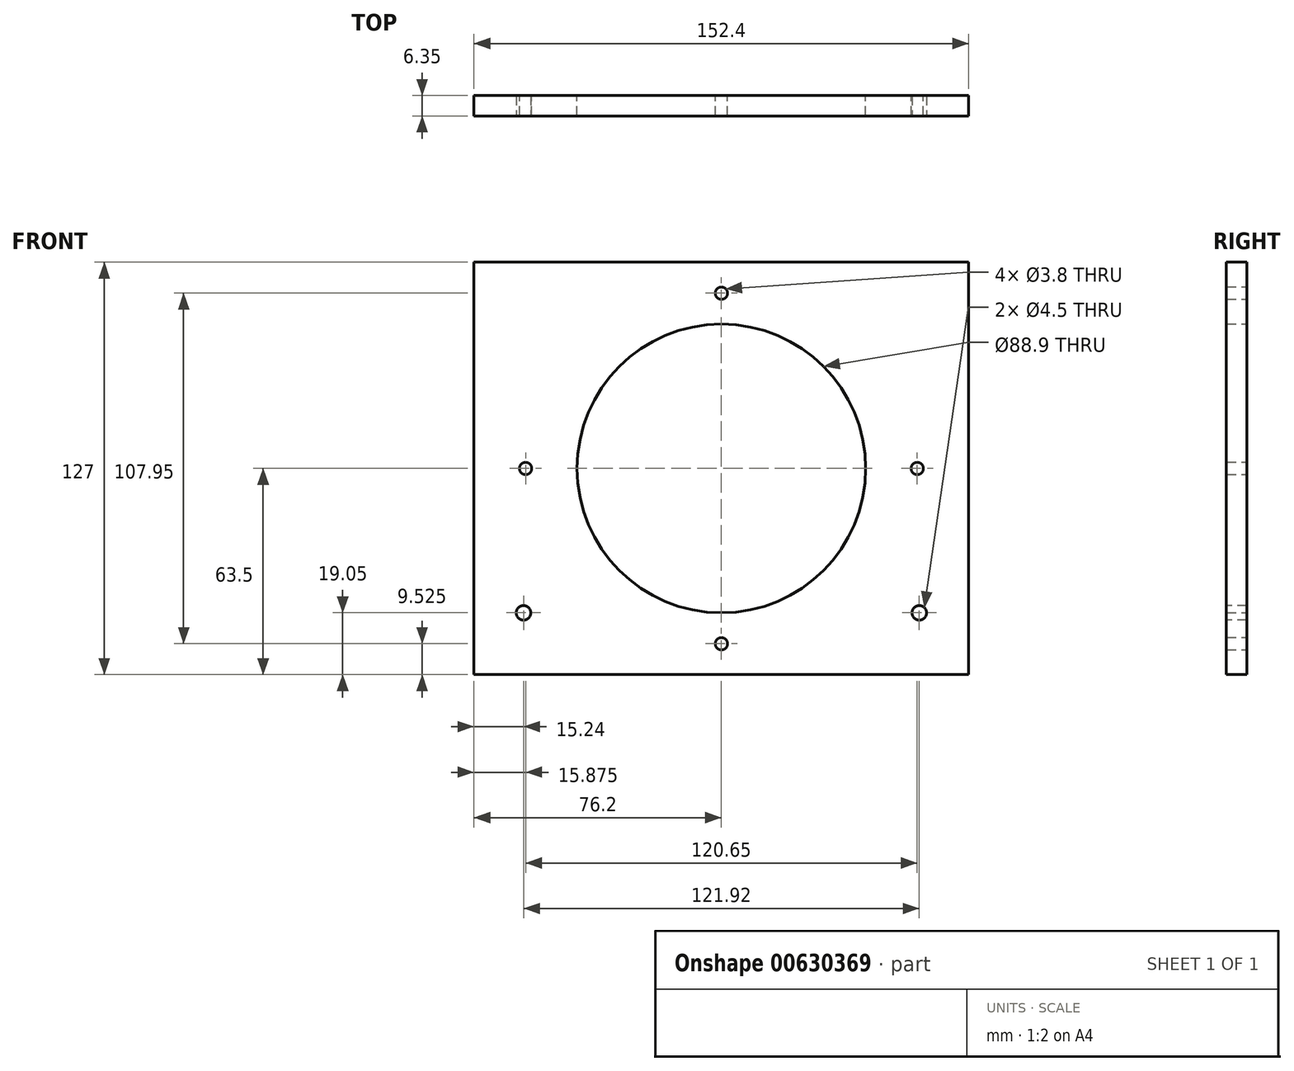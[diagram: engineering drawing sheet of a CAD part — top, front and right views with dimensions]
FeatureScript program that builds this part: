
annotation { "Feature Type Name" : "Feature", "Feature Type Description" : "" }
export const myFeature = defineFeature(function(context is Context, id is Id, definition is map)
    precondition{}
    {
        {
            var Q0;
            Q0=qCreatedBy(makeId("Front.planeOp"),FACE);
            var sketch = newSketch(context, id + "F0", { "sketchPlane" : qUnion([Q0])});
            skCircle(sketch, "E0", {"center": v(0, 0) * mm, "radius": 44.45 * mm});
            skLineSegment(sketch, "E1.bottom", {"start": v(-76.2, 63.5) * mm, "end": v(76.2, 63.5) * mm});
            skLineSegment(sketch, "E1.top", {"start": v(-76.2, -63.5) * mm, "end": v(76.2, -63.5) * mm});
            skLineSegment(sketch, "E1.left", {"start": v(-76.2, 63.5) * mm, "end": v(-76.2, -63.5) * mm});
            skLineSegment(sketch, "E1.right", {"start": v(76.2, 63.5) * mm, "end": v(76.2, -63.5) * mm});
            skSolve(sketch);
        }
        {
            var Q0;
            Q0 = qSketchRegion(id + "F0", true);
            extrude(context, id + "F1", {"entities" : qUnion([Q0]), "depth" : 6.35 * mm, "offsetDistance" : 25.4 * mm});
        }
        {
            var Q0;
            Q0=makeQuery(id+"F1.opExtrude","CAP_FACE",FACE,{"disambiguationData":[OSD([sQuery(id+"F0.wireOp",EDGE,"E0"),sQuery(id+"F0.wireOp",EDGE,"E1.bottom"),sQuery(id+"F0.wireOp",EDGE,"E1.top"),sQuery(id+"F0.wireOp",EDGE,"E1.left"),sQuery(id+"F0.wireOp",EDGE,"E1.right")])],"isStart":true});
            var sketch = newSketch(context, id + "F2", { "sketchPlane" : qUnion([Q0])});
            skSolve(sketch);
        }
        {
            var Q0;
            Q0=makeQuery(id+"F2.imprint","IMPRINT",FACE,{"disambiguationData":[TD([[makeQuery(id+"F2.imprint","IMPRINT",EDGE,{"derivedFrom":makeQuery(id+"F1.opExtrude","CAP_EDGE",EDGE,{"disambiguationData":[OSD([sQuery(id+"F0.wireOp",EDGE,"E0")])],"isStart":true})}),1.0]])]});
            var sketch = newSketch(context, id + "F3", { "sketchPlane" : qUnion([Q0])});
            skLineSegment(sketch, "E2", {"start": v(0, 63.5) * mm, "end": v(0, 44.45) * mm, "construction": true});
            skLineSegment(sketch, "E3", {"start": v(-76.2, 0) * mm, "end": v(-44.45, 0) * mm, "construction": true});
            skLineSegment(sketch, "E4", {"start": v(44.45, 0) * mm, "end": v(76.2, 0) * mm, "construction": true});
            skLineSegment(sketch, "E5", {"start": v(0, -63.5) * mm, "end": v(0, -44.45) * mm, "construction": true});
            skPoint(sketch, "E6", {"position": v(0, 53.98) * mm});
            skPoint(sketch, "E7", {"position": v(60.32, 0) * mm});
            skPoint(sketch, "E8", {"position": v(0, -53.98) * mm});
            skPoint(sketch, "E9", {"position": v(-60.32, 0) * mm});
            skSolve(sketch);
        }
        {
            var Q0;
            Q0=sQuery(id+"F3.wireOp",VERTEX,"E9");
            var Q1;
            Q1=sQuery(id+"F3.wireOp",VERTEX,"E6");
            var Q2;
            Q2=sQuery(id+"F3.wireOp",VERTEX,"E7");
            var Q3;
            Q3=sQuery(id+"F3.wireOp",VERTEX,"E8");
            var Q4;
            Q4=makeQuery(id+"F1.opExtrude","SWEPT_BODY",BODY,{"disambiguationData":[OSD([sQuery(id+"F0.wireOp",EDGE,"E0"),sQuery(id+"F0.wireOp",EDGE,"E1.bottom"),sQuery(id+"F0.wireOp",EDGE,"E1.top"),sQuery(id+"F0.wireOp",EDGE,"E1.left"),sQuery(id+"F0.wireOp",EDGE,"E1.right")])]});
            hole(context, id + "F4", {"style" : HoleStyle.SIMPLE, "endStyle" : HoleEndStyle.THROUGH, "standardTappedOrClearance" : lookupTablePath({ "standard" : "ANSI", "fit" : "Normal (ASME)", "size" : "#6", "type" : "Clearance" }), "standardBlindInLast" : lookupTablePath({ "fit" : "Free", "standard" : "ANSI", "size" : "#6", "type" : "Clearance" }), "holeDiameter" : 3.8 * mm, "majorDiameter" : 6.35 * mm, "isTappedThrough" : true, "tappedDepth" : 12.7 * mm, "tapClearance" : 3, "locations" : qUnion([Q0, Q1, Q2, Q3]), "scope" : qUnion([Q4])});
        }
        {
            var Q0;
            Q0=makeQuery(id+"F1.opExtrude","CAP_FACE",FACE,{"disambiguationData":[OSD([sQuery(id+"F0.wireOp",EDGE,"E0"),sQuery(id+"F0.wireOp",EDGE,"E1.bottom"),sQuery(id+"F0.wireOp",EDGE,"E1.top"),sQuery(id+"F0.wireOp",EDGE,"E1.left"),sQuery(id+"F0.wireOp",EDGE,"E1.right")])],"isStart":false});
            var sketch = newSketch(context, id + "F5", { "sketchPlane" : qUnion([Q0])});
            skLineSegment(sketch, "E10", {"start": v(-44.45, -63.5) * mm, "end": v(-44.45, -44.45) * mm, "construction": true});
            skLineSegment(sketch, "E11", {"start": v(-44.45, -44.45) * mm, "end": v(-60.96, -44.45) * mm, "construction": true});
            skLineSegment(sketch, "E12", {"start": v(44.45, -63.5) * mm, "end": v(44.45, -44.45) * mm, "construction": true});
            skLineSegment(sketch, "E13", {"start": v(44.45, -44.45) * mm, "end": v(60.96, -44.45) * mm, "construction": true});
            skLineSegment(sketch, "E14", {"start": v(0, 0) * mm, "end": v(0, -63.5) * mm, "construction": true});
            skLineSegment(sketch, "E15", {"start": v(0, -63.5) * mm, "end": v(-44.45, -63.5) * mm, "construction": true});
            skLineSegment(sketch, "E16", {"start": v(0, -63.5) * mm, "end": v(44.45, -63.5) * mm, "construction": true});
            skPoint(sketch, "E17", {"position": v(-60.96, -44.45) * mm});
            skPoint(sketch, "E18", {"position": v(60.96, -44.45) * mm});
            skSolve(sketch);
        }
        {
            var Q0;
            Q0=sQuery(id+"F5.wireOp",VERTEX,"E17");
            var Q1;
            Q1=sQuery(id+"F5.wireOp",VERTEX,"E18");
            var Q2;
            Q2=makeQuery(id+"F1.opExtrude","SWEPT_BODY",BODY,{"disambiguationData":[OSD([sQuery(id+"F0.wireOp",EDGE,"E0"),sQuery(id+"F0.wireOp",EDGE,"E1.bottom"),sQuery(id+"F0.wireOp",EDGE,"E1.top"),sQuery(id+"F0.wireOp",EDGE,"E1.left"),sQuery(id+"F0.wireOp",EDGE,"E1.right")])]});
            hole(context, id + "F6", {"style" : HoleStyle.SIMPLE, "endStyle" : HoleEndStyle.THROUGH, "standardTappedOrClearance" : lookupTablePath({ "standard" : "ANSI", "fit" : "Normal (ASME)", "size" : "#8", "type" : "Clearance" }), "standardBlindInLast" : lookupTablePath({ "fit" : "Free", "standard" : "ANSI", "size" : "#8", "type" : "Clearance" }), "holeDiameter" : 4.5 * mm, "majorDiameter" : 6.35 * mm, "isTappedThrough" : true, "tappedDepth" : 12.7 * mm, "tapClearance" : 3, "locations" : qUnion([Q0, Q1]), "scope" : qUnion([Q2])});
        }
    });
